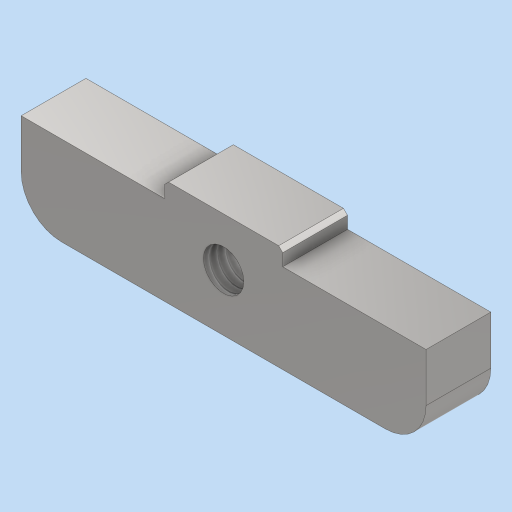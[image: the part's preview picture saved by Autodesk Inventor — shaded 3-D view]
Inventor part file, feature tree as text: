
AUTODESK INVENTOR PART (.ipt)
format: ipt  version: 2023 (Build 270158000, 158)  size: 200,192 bytes
history: native  units: mm
features: other x2, extrude x1
ambient origin geometry x8: Origin, YZ Plane, XZ Plane, XY Plane, X Axis, Y Axis, Z Axis, Center Point
bodies: Body1 (feature_tree)
feature tree (3):
  other  "實體1"
  extrude  "擠出1"  Depth=50.0mm
  other  "螺紋1"
